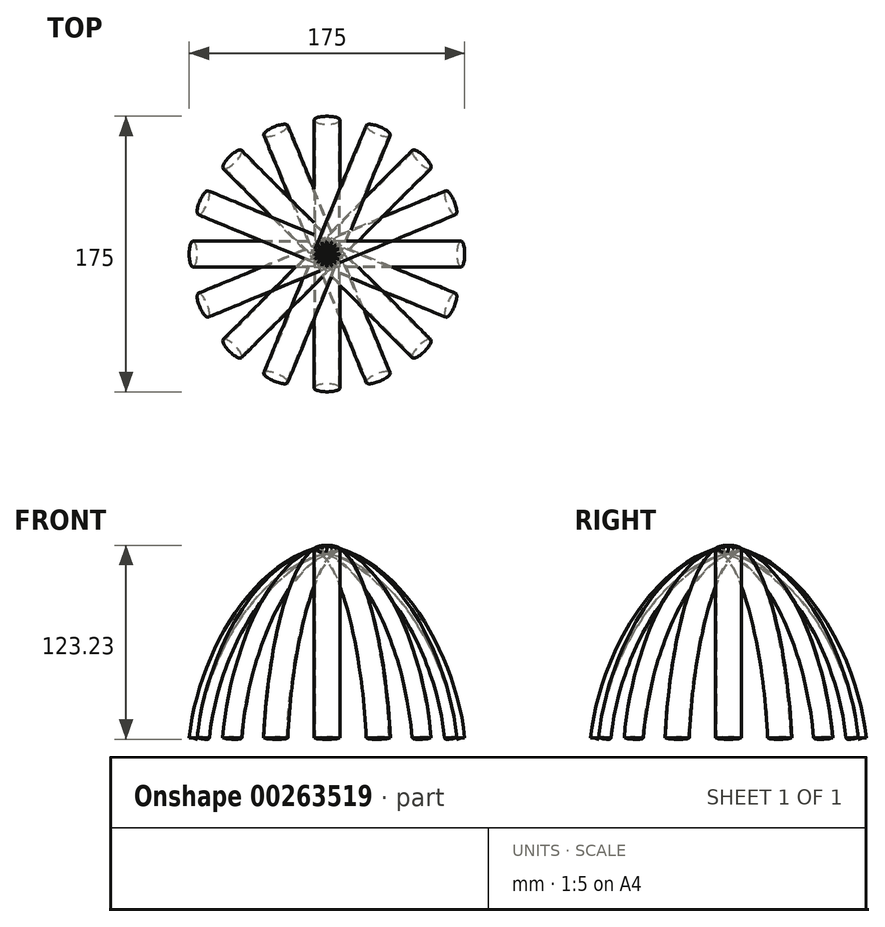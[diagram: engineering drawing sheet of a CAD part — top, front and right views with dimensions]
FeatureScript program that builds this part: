
annotation { "Feature Type Name" : "Feature", "Feature Type Description" : "" }
export const myFeature = defineFeature(function(context is Context, id is Id, definition is map)
    precondition{}
    {
        {
            var Q0;
            Q0=qCreatedBy(makeId("Top.planeOp"),FACE);
            var sketch = newSketch(context, id + "F0", { "sketchPlane" : qUnion([Q0])});
            skCircle(sketch, "E0", {"center": v(0, 0) * mm, "radius": 85 * mm, "construction": true});
            skLineSegment(sketch, "E1", {"start": v(-101.2, 0) * mm, "end": v(103.11, 0) * mm, "construction": true});
            skLineSegment(sketch, "E2", {"start": v(-85, 6.77) * mm, "end": v(-85, -8.23) * mm, "construction": true});
            skLineSegment(sketch, "E3", {"start": v(-87.5, 0) * mm, "end": v(-82.5, 0) * mm, "construction": true});
            skEllipse(sketch, "E4", {"center": v(-85, 0) * mm, "majorRadius": 8.23 * mm, "minorRadius": 2.5 * mm, "majorAxis": v(0, -1)});
            skSolve(sketch);
        }
        {
            var Q0;
            Q0=qCreatedBy(makeId("Right.planeOp"),FACE);
            var sketch = newSketch(context, id + "F1", { "sketchPlane" : qUnion([Q0])});
            skLineSegment(sketch, "E5", {"start": v(0, 120) * mm, "end": v(0, -120) * mm, "construction": true});
            skLineSegment(sketch, "E6", {"start": v(-7.5, 120) * mm, "end": v(7.5, 120) * mm, "construction": true});
            skEllipse(sketch, "E7", {"center": v(0, 120) * mm, "majorRadius": 7.5 * mm, "minorRadius": 2.5 * mm, "majorAxis": v(1, 0)});
            skLineSegment(sketch, "E8", {"start": v(0, 122.5) * mm, "end": v(0, 117.5) * mm, "construction": true});
            skSolve(sketch);
        }
        {
            var Q0;
            Q0=qCreatedBy(makeId("Front.planeOp"),FACE);
            var sketch = newSketch(context, id + "F2", { "sketchPlane" : qUnion([Q0])});
            skPoint(sketch, "E9.0", {"position": v(-85, 0) * mm});
            skPoint(sketch, "E10.0", {"position": v(0, 120) * mm});
            skFitSpline(sketch, "E11", {"points": [v(0, 120) * mm, v(-85, 0) * mm], "startDerivative": vector(-150, -30) * mm, "endDerivative": vector(-13.43, -135) * mm});
            skSolve(sketch);
        }
        {
            var Q0;
            Q0=makeQuery(id+"F1.imprint","IMPRINT",FACE,{"disambiguationData":[TD([[makeQuery(id+"F1.imprint","IMPRINT",EDGE,{"derivedFrom":sQuery(id+"F1.wireOp",EDGE,"E7")}),1.0]])]});
            var Q1;
            Q1=makeQuery(id+"F0.imprint","IMPRINT",FACE,{"disambiguationData":[TD([[makeQuery(id+"F0.imprint","IMPRINT",EDGE,{"derivedFrom":sQuery(id+"F0.wireOp",EDGE,"E4")}),1.0]])]});
            var Q2;
            Q2=sQuery(id+"F2.wireOp",EDGE,"E11");
            sweep(context, id + "F3", {"profiles" : qUnion([Q0, Q1]), "path" : qUnion([Q2])});
        }
        {
            var Q0;
            Q0=makeQuery(id+"F3.opSweep","SWEPT_BODY",BODY,{"disambiguationData":[OSD([sQuery(id+"F1.wireOp",EDGE,"E7"),sQuery(id+"F2.wireOp",EDGE,"E11")])]});
            var Q1;
            Q1=makeQuery(id+"F3.opSweep","SWEPT_BODY",BODY,{"disambiguationData":[OSD([sQuery(id+"F0.wireOp",EDGE,"E4"),sQuery(id+"F2.wireOp",EDGE,"E11")])]});
            var Q2;
            Q2=sQuery(id+"F0.wireOp",EDGE,"E0");
            circularPattern(context, id + "F4", {"entities" : qUnion([Q0, Q1]), "axis" : qUnion([Q2]), "angle" : 360 * degree, "instanceCount" : 16, "equalSpace" : true});
        }
    });
